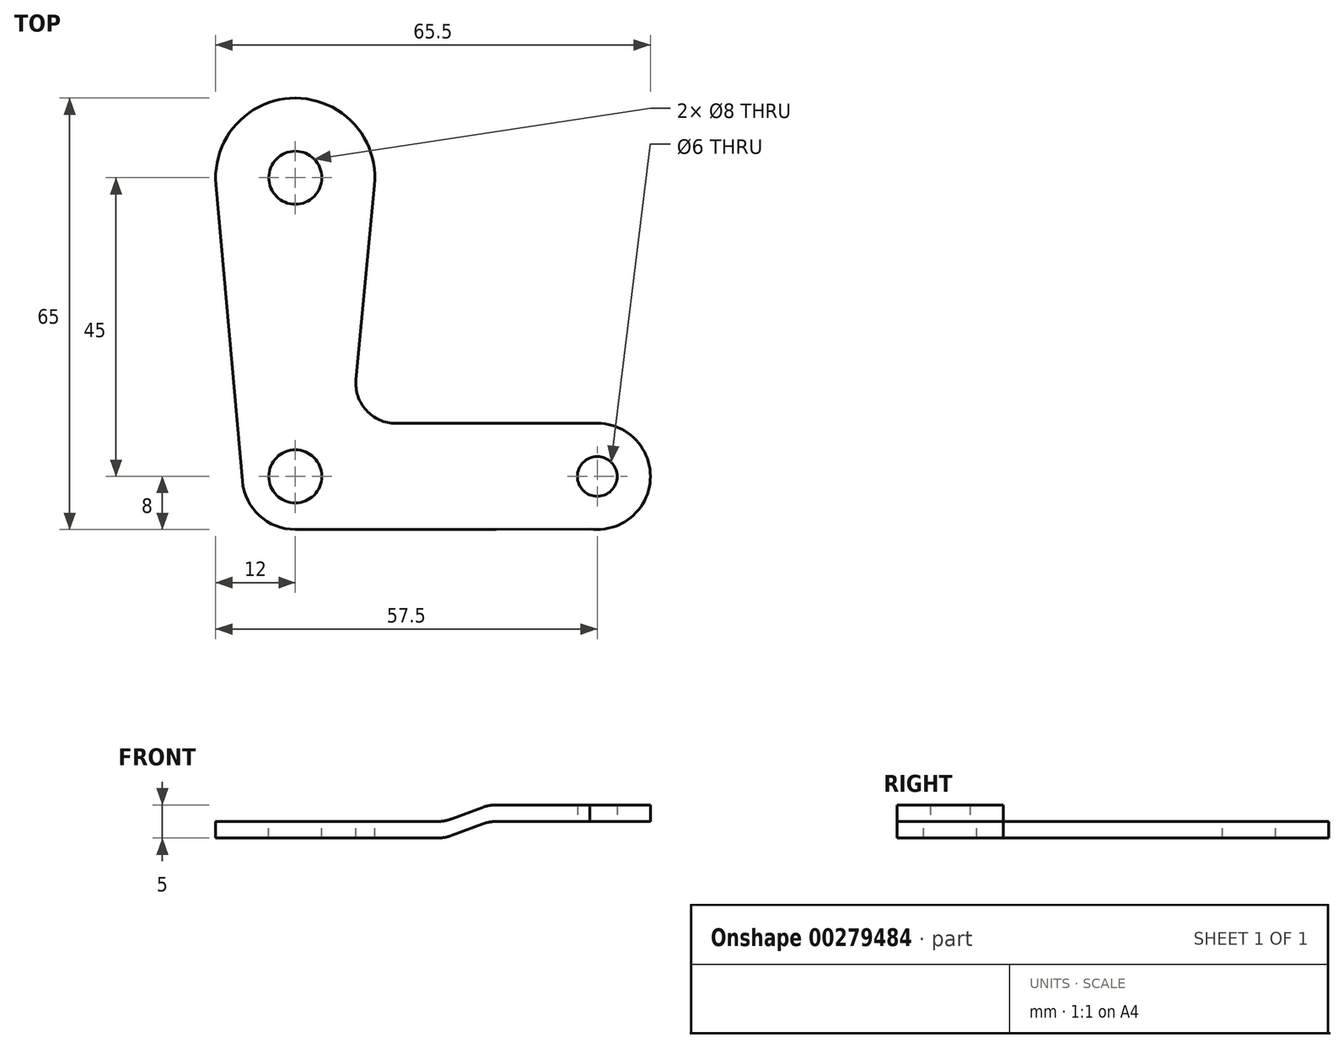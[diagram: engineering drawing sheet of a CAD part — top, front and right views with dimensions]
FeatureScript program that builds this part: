
annotation { "Feature Type Name" : "Feature", "Feature Type Description" : "" }
export const myFeature = defineFeature(function(context is Context, id is Id, definition is map)
    precondition{}
    {
        {
            var Q0;
            Q0=qCreatedBy(makeId("Top.planeOp"),FACE);
            var sketch = newSketch(context, id + "F0", { "sketchPlane" : qUnion([Q0])});
            skCircle(sketch, "E0", {"center": v(0, 0) * mm, "radius": 4 * mm});
            skCircle(sketch, "E1", {"center": v(0, 45) * mm, "radius": 4 * mm});
            skArc(sketch, "E2", {"start": v(11.95, 43.86) * mm, "mid": v(0.04, 57) * mm, "end": v(-11.95, 43.93) * mm});
            skArc(sketch, "E3", {"start": v(-7.97, -0.71) * mm, "mid": v(-5.4, -5.9) * mm, "end": v(0, -8) * mm});
            skLineSegment(sketch, "E4", {"start": v(-11.95, 43.93) * mm, "end": v(-7.97, -0.71) * mm});
            skLineSegment(sketch, "E5", {"start": v(0, -8) * mm, "end": v(22.5, -8) * mm});
            skLineSegment(sketch, "E6", {"start": v(11.95, 43.86) * mm, "end": v(9.16, 14.57) * mm});
            skLineSegment(sketch, "E7", {"start": v(15.13, 8) * mm, "end": v(22.5, 8) * mm});
            skPoint(sketch, "E8.visualSharp", {"position": v(8.53, 8) * mm});
            skArc(sketch, "E8.filletArc", {"start": v(9.16, 14.57) * mm, "mid": v(10.7, 9.96) * mm, "end": v(15.13, 8) * mm});
            skLineSegment(sketch, "E9", {"start": v(22.5, 8) * mm, "end": v(22.5, -8) * mm});
            skSolve(sketch);
        }
        {
            var Q0;
            Q0 = qSketchRegion(id + "F0", true);
            extrude(context, id + "F1", {"entities" : qUnion([Q0]), "oppositeDirection" : true, "depth" : 2.5 * mm});
        }
        {
            var Q0;
            Q0=makeQuery(id+"F1.opExtrude","CAP_FACE",FACE,{"disambiguationData":[OSD([sQuery(id+"F0.wireOp",EDGE,"E0"),sQuery(id+"F0.wireOp",EDGE,"E1"),sQuery(id+"F0.wireOp",EDGE,"E2"),sQuery(id+"F0.wireOp",EDGE,"E3"),sQuery(id+"F0.wireOp",EDGE,"E4"),sQuery(id+"F0.wireOp",EDGE,"E5"),sQuery(id+"F0.wireOp",EDGE,"E6"),sQuery(id+"F0.wireOp",EDGE,"E7"),sQuery(id+"F0.wireOp",EDGE,"E8.filletArc"),sQuery(id+"F0.wireOp",EDGE,"E9")])],"isStart":false});
            cPlane(context, id + "F2", {"entities" : qUnion([Q0]), "cplaneType" : CPlaneType.OFFSET, "offset" : 2.5 * mm, "oppositeDirection" : true, "width" : 150 * mm, "height" : 150 * mm});
        }
        {
            var Q0;
            Q0=qCreatedBy(id+"F2.planeOp",FACE);
            var sketch = newSketch(context, id + "F3", { "sketchPlane" : qUnion([Q0])});
            skCircle(sketch, "E10.0", {"center": v(0, 0) * mm, "radius": 4 * mm, "construction": true});
            skLineSegment(sketch, "E11.0", {"start": v(22.5, -8) * mm, "end": v(22.5, 8) * mm, "construction": true});
            skCircle(sketch, "E12", {"center": v(45.5, 0) * mm, "radius": 3 * mm});
            skArc(sketch, "E13", {"start": v(45.5, -8) * mm, "mid": v(53.48, 0.56) * mm, "end": v(44.39, 7.92) * mm});
            skLineSegment(sketch, "E14", {"start": v(29.17, 7.98) * mm, "end": v(46.67, 7.91) * mm});
            skLineSegment(sketch, "E15", {"start": v(29.17, -8) * mm, "end": v(45.5, -8) * mm});
            skLineSegment(sketch, "E16", {"start": v(22.5, 8) * mm, "end": v(22.5, -8) * mm, "construction": true});
            skLineSegment(sketch, "E17", {"start": v(29.17, 7.98) * mm, "end": v(29.17, -8) * mm});
            skSolve(sketch);
        }
        {
            var Q0;
            Q0 = qSketchRegion(id + "F3", true);
            extrude(context, id + "F4", {"entities" : qUnion([Q0]), "oppositeDirection" : true, "depth" : 2.5 * mm});
        }
        {
            var Q0;
            Q0=makeQuery(id+"F1.opExtrude","SWEPT_FACE",FACE,{"disambiguationData":[OSD([sQuery(id+"F0.wireOp",EDGE,"E9")])]});
            var Q1;
            Q1=makeQuery(id+"F4.opExtrude","SWEPT_FACE",FACE,{"disambiguationData":[OSD([sQuery(id+"F3.wireOp",EDGE,"E17")])]});
            loft(context, id + "F5", {"sheetProfilesArray" : [{ "sheetProfileEntities" : qUnion([Q0]) }, { "sheetProfileEntities" : qUnion([Q1]) }]});
        }
        {
            var Q0;
            Q0=makeQuery(id+"F1.opExtrude","SWEPT_BODY",BODY,{"disambiguationData":[OSD([sQuery(id+"F0.wireOp",EDGE,"E0"),sQuery(id+"F0.wireOp",EDGE,"E1"),sQuery(id+"F0.wireOp",EDGE,"E2"),sQuery(id+"F0.wireOp",EDGE,"E3"),sQuery(id+"F0.wireOp",EDGE,"E4"),sQuery(id+"F0.wireOp",EDGE,"E5"),sQuery(id+"F0.wireOp",EDGE,"E6"),sQuery(id+"F0.wireOp",EDGE,"E7"),sQuery(id+"F0.wireOp",EDGE,"E8.filletArc"),sQuery(id+"F0.wireOp",EDGE,"E9")])]});
            var Q1;
            Q1=makeQuery(id+"F4.opExtrude","SWEPT_BODY",BODY,{"disambiguationData":[OSD([sQuery(id+"F3.wireOp",EDGE,"E12"),sQuery(id+"F3.wireOp",EDGE,"E13"),sQuery(id+"F3.wireOp",EDGE,"E14"),sQuery(id+"F3.wireOp",EDGE,"E15"),sQuery(id+"F3.wireOp",EDGE,"E17")])]});
            var Q2;
            Q2=makeQuery(id+"F5.opLoft","SWEPT_BODY",BODY,{"disambiguationData":[OSD([sQuery(id+"F0.wireOp",EDGE,"E9"),sQuery(id+"F3.wireOp",EDGE,"E17")])]});
            booleanBodies(context, id + "F6", {"operationType" : BooleanOperationType.UNION, "tools" : qUnion([Q0, Q1, Q2])});
        }
        {
            var Q0;
            {var subQ0=sQuery(id+"F0.wireOp",EDGE,"E9");var subQ1=makeQuery(id+"F1.opExtrude","CAP_EDGE",EDGE,{"disambiguationData":[OSD([subQ0])],"isStart":true});var subQ2=sQuery(id+"F0.wireOp",EDGE,"E7");var subQ3=sQuery(id+"F0.wireOp",EDGE,"E5");Q0=makeQuery(id+"F6.opBoolean","MERGE",EDGE,{"derivedFrom":[subQ1,makeQuery(id+"F5.opLoft","MID_CAP_EDGE",EDGE,{"disambiguationData":[OSD([subQ3,subQ2,subQ0]),TDD([makeQuery(id+"F1.opExtrude","CAP_VERTEX",VERTEX,{"disambiguationData":[OSD([subQ3,subQ0])],"isStart":true}),makeQuery(id+"F1.opExtrude","CAP_VERTEX",VERTEX,{"disambiguationData":[OSD([subQ2,subQ0])],"isStart":true}),subQ1])],"capPos":0.0})]});}
            var Q1;
            {var subQ0=sQuery(id+"F3.wireOp",EDGE,"E17");var subQ1=makeQuery(id+"F4.opExtrude","CAP_EDGE",EDGE,{"disambiguationData":[OSD([subQ0])],"isStart":false});var subQ2=sQuery(id+"F3.wireOp",EDGE,"E15");var subQ3=sQuery(id+"F3.wireOp",EDGE,"E14");Q1=makeQuery(id+"F6.opBoolean","MERGE",EDGE,{"derivedFrom":[subQ1,makeQuery(id+"F5.opLoft","MID_CAP_EDGE",EDGE,{"disambiguationData":[OSD([subQ3,subQ2,subQ0]),TDD([makeQuery(id+"F4.opExtrude","CAP_VERTEX",VERTEX,{"disambiguationData":[OSD([subQ3,subQ0])],"isStart":false}),makeQuery(id+"F4.opExtrude","CAP_VERTEX",VERTEX,{"disambiguationData":[OSD([subQ2,subQ0])],"isStart":false}),subQ1])],"capPos":1.0})]});}
            fillet(context, id + "F7", {"entities" : qUnion([Q0, Q1]), "radius" : 6 * mm, "tangentPropagation" : true, "allowEdgeOverflow" : false});
        }
        {
            var Q0;
            {var subQ0=sQuery(id+"F3.wireOp",EDGE,"E17");var subQ1=makeQuery(id+"F4.opExtrude","CAP_EDGE",EDGE,{"disambiguationData":[OSD([subQ0])],"isStart":true});var subQ2=sQuery(id+"F3.wireOp",EDGE,"E15");var subQ3=sQuery(id+"F3.wireOp",EDGE,"E14");Q0=makeQuery(id+"F6.opBoolean","MERGE",EDGE,{"derivedFrom":[subQ1,makeQuery(id+"F5.opLoft","MID_CAP_EDGE",EDGE,{"disambiguationData":[OSD([subQ3,subQ2,subQ0]),TDD([makeQuery(id+"F4.opExtrude","CAP_VERTEX",VERTEX,{"disambiguationData":[OSD([subQ3,subQ0])],"isStart":true}),makeQuery(id+"F4.opExtrude","CAP_VERTEX",VERTEX,{"disambiguationData":[OSD([subQ2,subQ0])],"isStart":true}),subQ1])],"capPos":1.0})]});}
            var Q1;
            {var subQ0=sQuery(id+"F0.wireOp",EDGE,"E9");var subQ1=makeQuery(id+"F1.opExtrude","CAP_EDGE",EDGE,{"disambiguationData":[OSD([subQ0])],"isStart":false});var subQ2=sQuery(id+"F0.wireOp",EDGE,"E7");var subQ3=sQuery(id+"F0.wireOp",EDGE,"E5");Q1=makeQuery(id+"F6.opBoolean","MERGE",EDGE,{"derivedFrom":[subQ1,makeQuery(id+"F5.opLoft","MID_CAP_EDGE",EDGE,{"disambiguationData":[OSD([subQ3,subQ2,subQ0]),TDD([makeQuery(id+"F1.opExtrude","CAP_VERTEX",VERTEX,{"disambiguationData":[OSD([subQ3,subQ0])],"isStart":false}),makeQuery(id+"F1.opExtrude","CAP_VERTEX",VERTEX,{"disambiguationData":[OSD([subQ2,subQ0])],"isStart":false}),subQ1])],"capPos":0.0})]});}
            fillet(context, id + "F8", {"entities" : qUnion([Q0, Q1]), "radius" : 6 * mm, "tangentPropagation" : true, "allowEdgeOverflow" : false});
        }
    });
